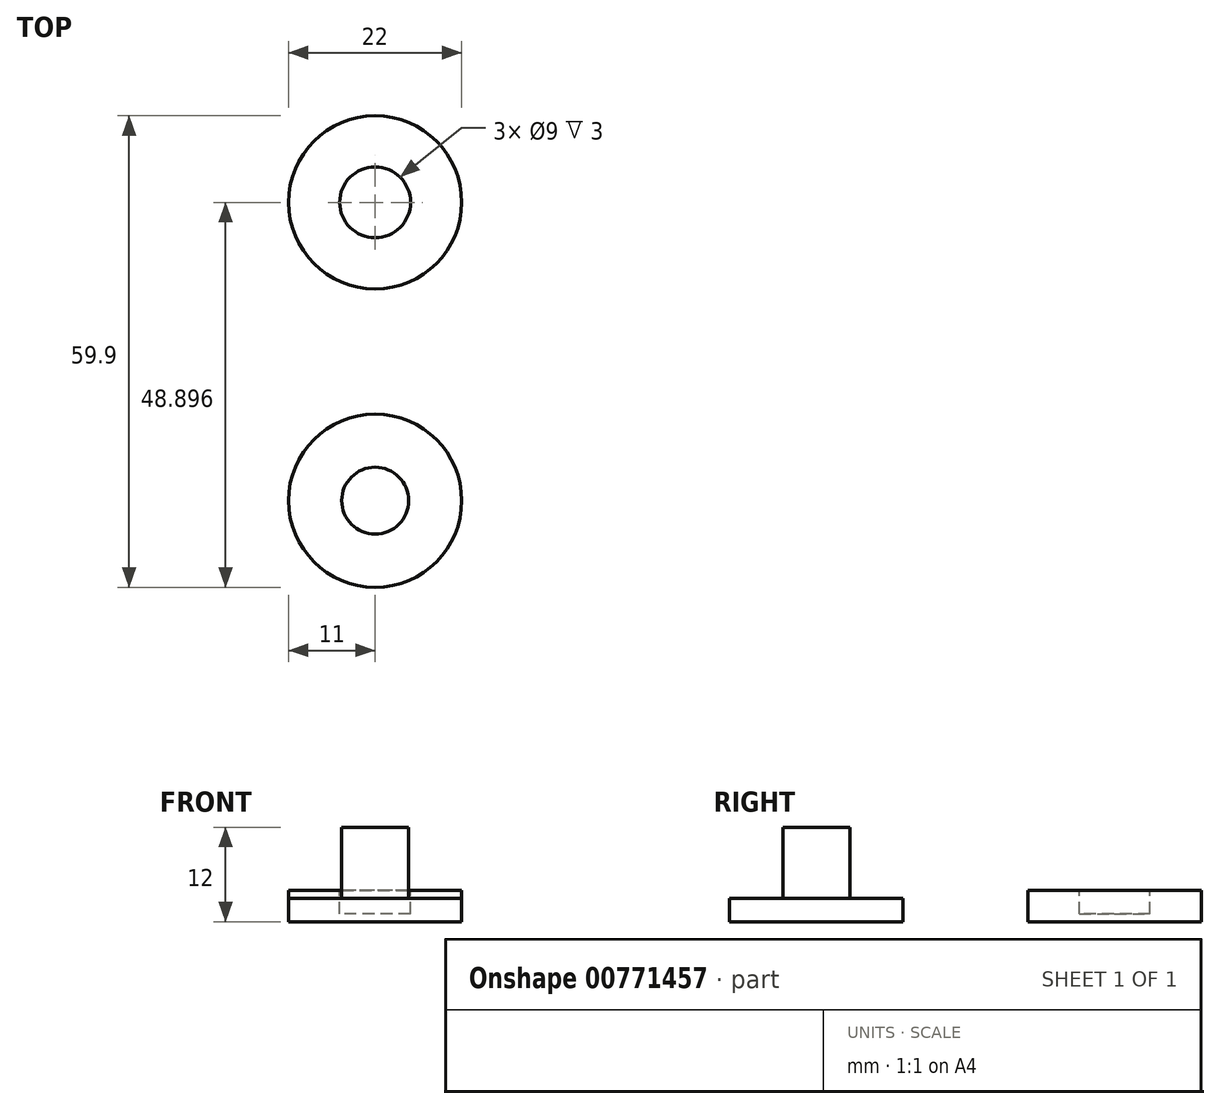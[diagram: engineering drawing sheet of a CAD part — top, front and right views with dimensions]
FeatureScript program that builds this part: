
annotation { "Feature Type Name" : "Feature", "Feature Type Description" : "" }
export const myFeature = defineFeature(function(context is Context, id is Id, definition is map)
    precondition{}
    {
        {
            var Q0;
            Q0=qCreatedBy(makeId("Top.planeOp"),FACE);
            var sketch = newSketch(context, id + "F0", { "sketchPlane" : qUnion([Q0])});
            skCircle(sketch, "E0", {"center": v(0, 0) * mm, "radius": 11 * mm});
            skSolve(sketch);
        }
        {
            var Q0;
            Q0=makeQuery(id+"F0.imprint","IMPRINT",FACE,{"disambiguationData":[TD([[makeQuery(id+"F0.imprint","IMPRINT",EDGE,{"derivedFrom":sQuery(id+"F0.wireOp",EDGE,"E0")}),1.0]])]});
            extrude(context, id + "F1", {"entities" : qUnion([Q0]), "depth" : 3 * mm, "offsetDistance" : 25 * mm});
        }
        {
            var Q0;
            Q0=makeQuery(id+"F1.opExtrude","CAP_FACE",FACE,{"disambiguationData":[OSD([sQuery(id+"F0.wireOp",EDGE,"E0")])],"isStart":false});
            var sketch = newSketch(context, id + "F2", { "sketchPlane" : qUnion([Q0])});
            skCircle(sketch, "E1", {"center": v(0, 0) * mm, "radius": 4.25 * mm});
            skSolve(sketch);
        }
        {
            var Q0;
            Q0=makeQuery(id+"F2.imprint","IMPRINT",FACE,{"disambiguationData":[TD([[makeQuery(id+"F2.imprint","IMPRINT",EDGE,{"derivedFrom":sQuery(id+"F2.wireOp",EDGE,"E1")}),1.0]])]});
            extrude(context, id + "F3", {"entities" : qUnion([Q0]), "operationType" : NewBodyOperationType.ADD, "depth" : 9 * mm, "offsetDistance" : 25 * mm});
        }
        {
            var Q0;
            Q0=qCreatedBy(makeId("Top.planeOp"),FACE);
            var sketch = newSketch(context, id + "F4", { "sketchPlane" : qUnion([Q0])});
            skCircle(sketch, "E2", {"center": v(0, 37.9) * mm, "radius": 11 * mm});
            skSolve(sketch);
        }
        {
            var Q0;
            Q0=makeQuery(id+"F4.imprint","IMPRINT",FACE,{"disambiguationData":[TD([[makeQuery(id+"F4.imprint","IMPRINT",EDGE,{"derivedFrom":sQuery(id+"F4.wireOp",EDGE,"E2")}),1.0]])]});
            extrude(context, id + "F5", {"entities" : qUnion([Q0]), "depth" : 4 * mm, "offsetDistance" : 25 * mm});
        }
        {
            var Q0;
            Q0=makeQuery(id+"F5.opExtrude","CAP_FACE",FACE,{"disambiguationData":[OSD([sQuery(id+"F4.wireOp",EDGE,"E2")])],"isStart":false});
            var sketch = newSketch(context, id + "F6", { "sketchPlane" : qUnion([Q0])});
            skCircle(sketch, "E3", {"center": v(0, 37.9) * mm, "radius": 4.5 * mm});
            skSolve(sketch);
        }
        {
            var Q0;
            Q0=makeQuery(id+"F6.imprint","IMPRINT",FACE,{"disambiguationData":[TD([[makeQuery(id+"F6.imprint","IMPRINT",EDGE,{"derivedFrom":sQuery(id+"F6.wireOp",EDGE,"E3")}),1.0]])]});
            extrude(context, id + "F7", {"entities" : qUnion([Q0]), "operationType" : NewBodyOperationType.REMOVE, "oppositeDirection" : true, "depth" : 3 * mm, "offsetDistance" : 25 * mm});
        }
    });
